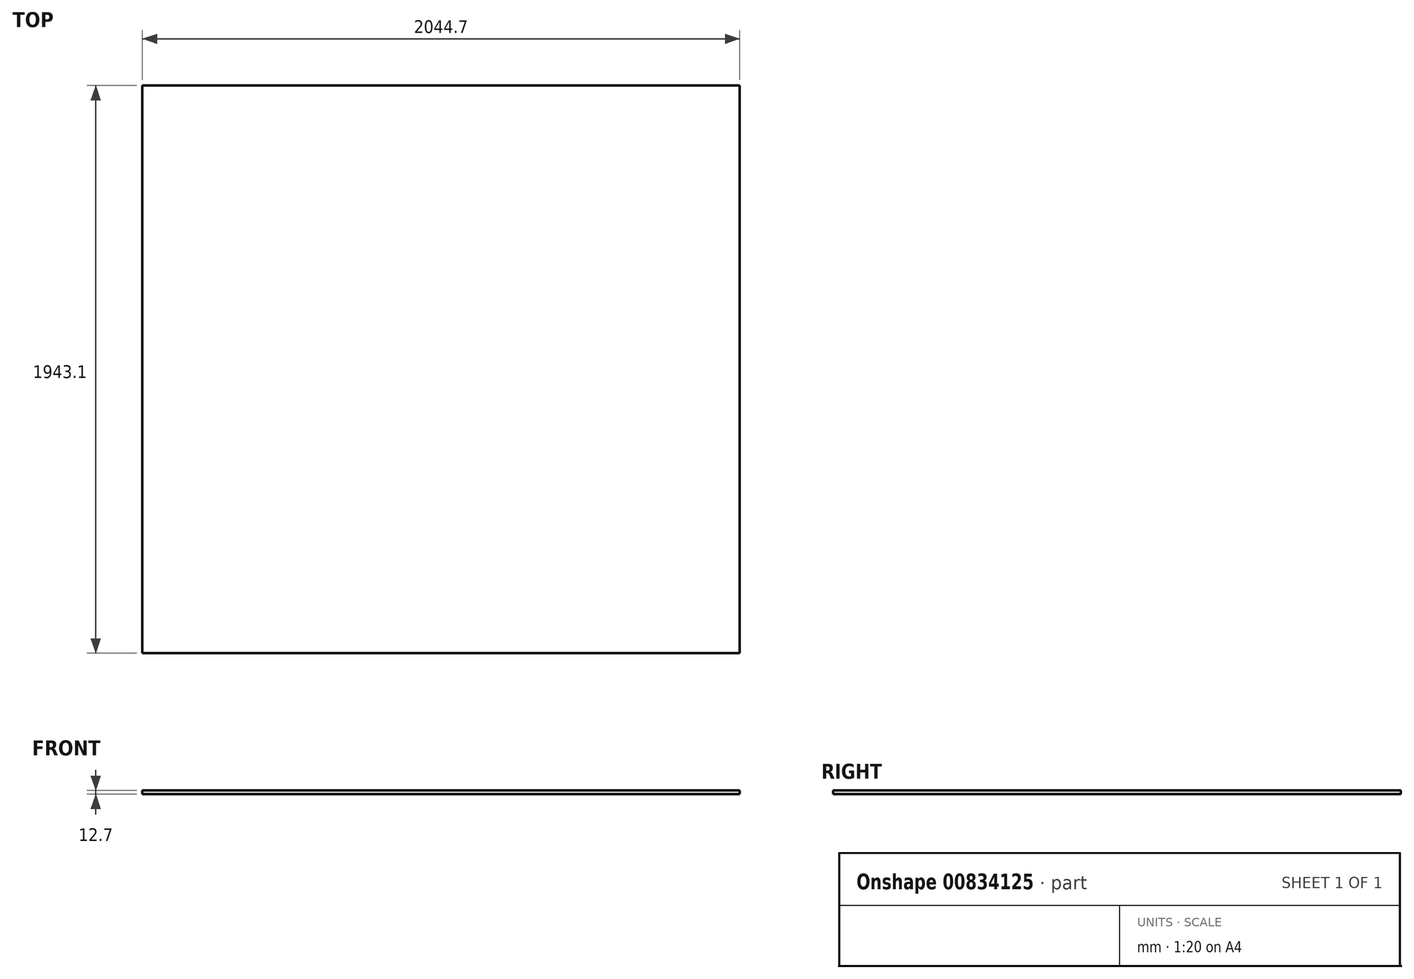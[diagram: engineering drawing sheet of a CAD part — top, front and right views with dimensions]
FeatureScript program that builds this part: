
annotation { "Feature Type Name" : "Feature", "Feature Type Description" : "" }
export const myFeature = defineFeature(function(context is Context, id is Id, definition is map)
    precondition{}
    {
        {
            var Q0;
            Q0=qCreatedBy(makeId("Top.planeOp"),FACE);
            var sketch = newSketch(context, id + "F0", { "sketchPlane" : qUnion([Q0])});
            skLineSegment(sketch, "E0.rect.bottom", {"start": v(1022.35, -971.55) * mm, "end": v(-1022.35, -971.55) * mm});
            skLineSegment(sketch, "E0.rect.top", {"start": v(1022.35, 971.55) * mm, "end": v(-1022.35, 971.55) * mm});
            skLineSegment(sketch, "E0.rect.left", {"start": v(1022.35, -971.55) * mm, "end": v(1022.35, 971.55) * mm});
            skLineSegment(sketch, "E0.rect.right", {"start": v(-1022.35, -971.55) * mm, "end": v(-1022.35, 971.55) * mm});
            skPoint(sketch, "E0.rect.middle", {"position": v(0, 0) * mm});
            skSolve(sketch);
        }
        {
            var Q0;
            Q0=qSketchRegion(id+"F0",true);
            extrude(context, id + "F1", {"entities" : qUnion([Q0]), "depth" : 12.7 * mm});
        }
    });
